FCSTD DOCUMENT  (FreeCAD 0.16R)
Label: cut_camera_stand
License: All rights reserved
LicenseURL: http://en.wikipedia.org/wiki/All_rights_reserved
objects: Part::Part2DObjectPython×7, Sketcher::SketchObject×1
note: 8 computed .brp shape members not serialized (recipe doc carries the construction recipe); baked Part::Feature solids carry a one-line shape summary decoded from their .brp

FEATURE [Part::Part2DObjectPython] Circle  label="outer_cut"  # Draft 2D object (typed FeaturePython)
  FirstAngle = 0
  LastAngle = 0
  MakeFace = false
  MapMode = -1
  Radius = 13
FEATURE [Part::Part2DObjectPython] Circle002  label="center_hole"  # Draft 2D object (typed FeaturePython)
  FirstAngle = 0
  LastAngle = 0
  MakeFace = false
  MapMode = -1
  Radius = 4.05
FEATURE [Part::Part2DObjectPython] Rectangle  # Draft 2D object (typed FeaturePython)
  ChamferSize = 0
  Columns = 1
  FilletRadius = 0
  Height = -14
  Length = 8.4
  MakeFace = true
  MapMode = -1
  Placement = pos=(-4.2,4.25,0) rot=(0,0,1;0rad)
  Rows = 1
FEATURE [Part::Part2DObjectPython] Arc  # Draft 2D object (typed FeaturePython)
  FirstAngle = -360
  LastAngle = -90
  MakeFace = true
  MapMode = -1
  Placement = pos=(-4.2,4.25,0) rot=(0,0,1;0rad)
  Radius = 0.8
FEATURE [Part::Part2DObjectPython] Arc001  # Draft 2D object (typed FeaturePython)
  FirstAngle = -90
  LastAngle = 180
  MakeFace = true
  MapMode = -1
  Placement = pos=(4.2,4.25,0) rot=(0,0,1;0rad)
  Radius = 0.8
FEATURE [Part::Part2DObjectPython] Arc002  # Draft 2D object (typed FeaturePython)
  FirstAngle = 92.7056
  LastAngle = 360
  MakeFace = true
  MapMode = -1
  Placement = pos=(-4.16446,-9.75,0) rot=(0,0,1;0rad)
  Radius = 0.8
FEATURE [Part::Part2DObjectPython] Arc003  # Draft 2D object (typed FeaturePython)
  FirstAngle = -180
  LastAngle = 90
  MakeFace = true
  MapMode = -1
  Placement = pos=(4.2,-9.75,0) rot=(0,0,1;0rad)
  Radius = 0.8
FEATURE [Sketcher::SketchObject] Sketch  label="base_depth2.5"
  sketch-geometry (8):
    g0: ArcOfCircle CenterX=4.2163 CenterY=-9.73014 CenterZ=0 NormalX=0 NormalY=0 NormalZ=1 Radius=0.795082 StartAngle=3.15583 EndAngle=7.85737
    g1: LineSegment StartX=-3.39159 StartY=4.24592 StartZ=0 EndX=3.41244 EndY=4.24592 EndZ=0
    g2: LineSegment StartX=4.21361 StartY=3.45077 StartZ=0 EndX=4.21361 EndY=-8.93506 EndZ=0
    g3: LineSegment StartX=3.4213 StartY=-9.74146 StartZ=0 EndX=-3.36548 EndY=-9.74146 EndZ=0
    g4: LineSegment StartX=-4.20196 StartY=-8.94829 StartZ=0 EndX=-4.20196 EndY=3.44675 EndZ=0
    g5: ArcOfCircle CenterX=4.20723 CenterY=4.24554 CenterZ=0 NormalX=0 NormalY=0 NormalZ=1 Radius=0.794792 StartAngle=4.72041 EndAngle=9.4243
    g6: ArcOfCircle CenterX=-4.19357 CenterY=4.24868 CenterZ=0 NormalX=0 NormalY=0 NormalZ=1 Radius=0.801977 StartAngle=6.27974 EndAngle=10.9851
    g7: ArcOfCircle CenterX=-4.16389 CenterY=-9.74581 CenterZ=0 NormalX=0 NormalY=0 NormalZ=1 Radius=0.798422 StartAngle=1.61848 EndAngle=6.28863
  constraints (12):
    c: Horizontal(g1)
    c: Vertical(g2)
    c: Horizontal(g3)
    c: Vertical(g4)
    c: Coincident(g1,g6)
    c: Coincident(g1,g5)
    c: Coincident(g4,g6)
    c: Coincident(g2,g5)
    c: Coincident(g3,g7)
    c: Coincident(g4,g7)
    c: Coincident(g0,g2)
    c: Coincident(g3,g0)
